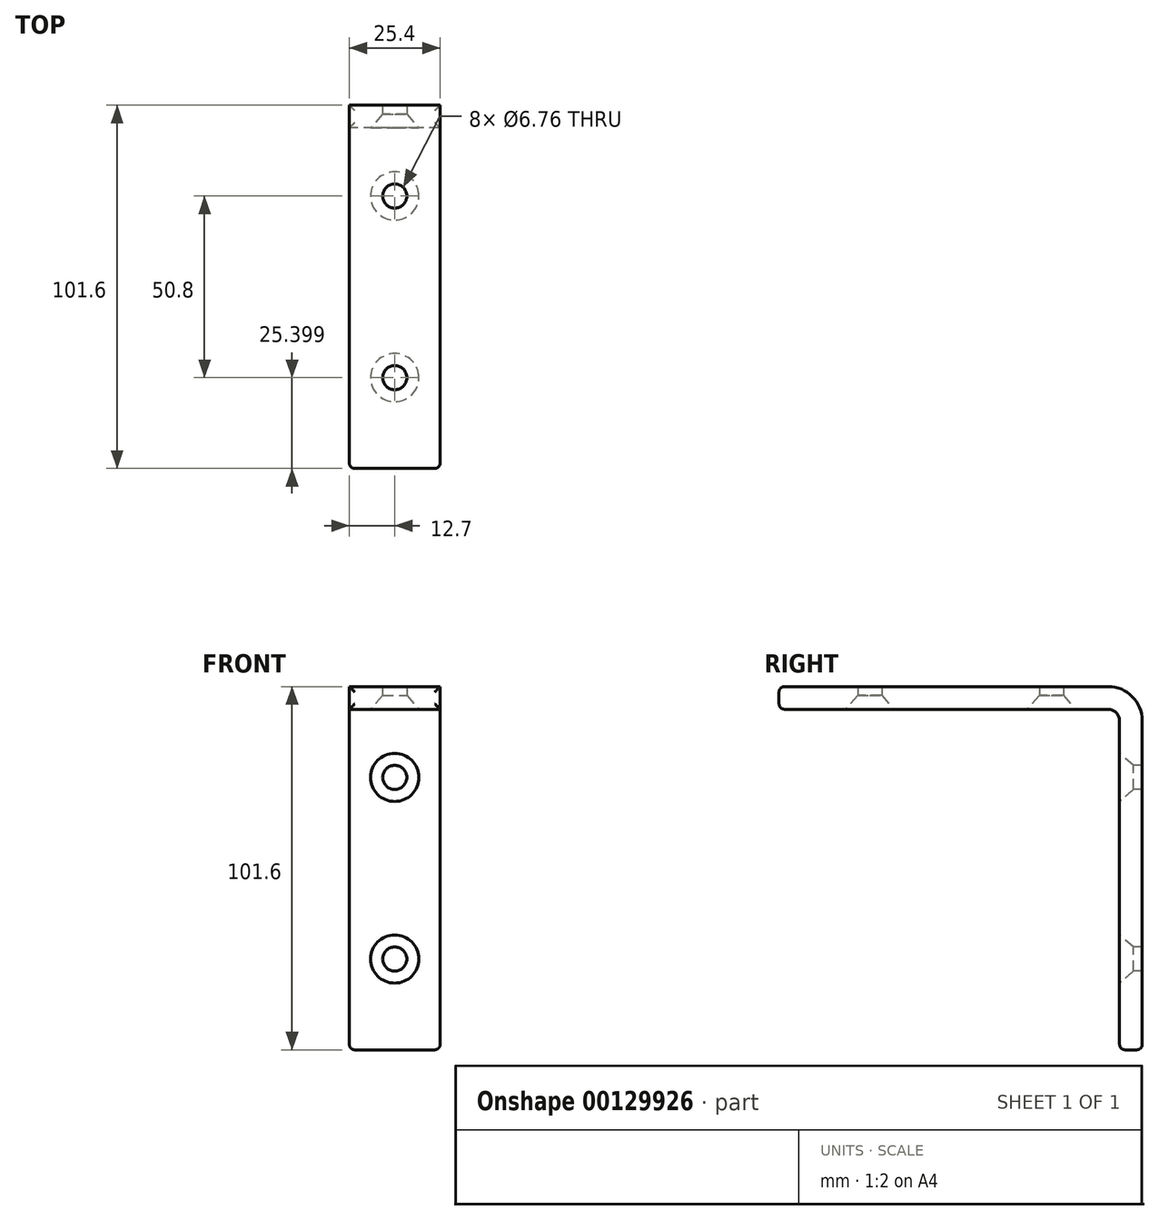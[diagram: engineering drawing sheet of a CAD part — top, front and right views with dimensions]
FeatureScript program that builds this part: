
annotation { "Feature Type Name" : "Feature", "Feature Type Description" : "" }
export const myFeature = defineFeature(function(context is Context, id is Id, definition is map)
    precondition{}
    {
        {
            var Q0;
            Q0=qCreatedBy(makeId("Right.planeOp"),FACE);
            var sketch = newSketch(context, id + "F0", { "sketchPlane" : qUnion([Q0])});
            skLineSegment(sketch, "E0", {"start": v(-36.08, 9.65) * mm, "end": v(59.17, 9.65) * mm});
            skLineSegment(sketch, "E1", {"start": v(59.17, 9.65) * mm, "end": v(59.17, -85.6) * mm});
            skLineSegment(sketch, "E2.0", {"start": v(-36.08, 16) * mm, "end": v(65.52, 16) * mm});
            skLineSegment(sketch, "E3.0", {"start": v(65.52, 16) * mm, "end": v(65.52, -85.6) * mm});
            skLineSegment(sketch, "E4", {"start": v(-36.08, 16) * mm, "end": v(-36.08, 9.65) * mm});
            skLineSegment(sketch, "E5", {"start": v(59.17, -85.6) * mm, "end": v(65.52, -85.6) * mm});
            skSolve(sketch);
        }
        {
            var Q0;
            Q0=makeQuery(id+"F0.imprint","IMPRINT",FACE,{"disambiguationData":[TD([[makeQuery(id+"F0.imprint","IMPRINT",EDGE,{"derivedFrom":sQuery(id+"F0.wireOp",EDGE,"E0")}),1.0]])]});
            extrude(context, id + "F1", {"entities" : qUnion([Q0]), "endBound" : BoundingType.SYMMETRIC, "depth" : 25.4 * mm});
        }
        {
            var Q0;
            Q0=makeQuery(id+"F1.opExtrude","SWEPT_FACE",FACE,{"disambiguationData":[OSD([sQuery(id+"F0.wireOp",EDGE,"E1")])]});
            var sketch = newSketch(context, id + "F2", { "sketchPlane" : qUnion([Q0])});
            skCircle(sketch, "E6", {"center": v(0, -9.4) * mm, "radius": 2.32 * mm});
            skCircle(sketch, "E7", {"center": v(0, -60.2) * mm, "radius": 3.49 * mm});
            skSolve(sketch);
        }
        {
            var Q0;
            Q0=sQuery(id+"F2.wireOp",VERTEX,"E6.center");
            var Q1;
            Q1=sQuery(id+"F2.wireOp",VERTEX,"E7.center");
            var Q2;
            Q2=makeQuery(id+"F1.opExtrude","SWEPT_BODY",BODY,{"disambiguationData":[OSD([sQuery(id+"F0.wireOp",EDGE,"E0"),sQuery(id+"F0.wireOp",EDGE,"E1"),sQuery(id+"F0.wireOp",EDGE,"E2.0"),sQuery(id+"F0.wireOp",EDGE,"E3.0"),sQuery(id+"F0.wireOp",EDGE,"E4"),sQuery(id+"F0.wireOp",EDGE,"E5")])]});
            hole(context, id + "F3", {"style" : HoleStyle.C_SINK, "endStyle" : HoleEndStyle.THROUGH, "standardTappedOrClearance" : lookupTablePath({ "standard" : "ANSI", "fit" : "Normal (ASME)", "size" : "1/4", "type" : "Clearance" }), "standardBlindInLast" : lookupTablePath({ "fit" : "Free", "standard" : "ANSI", "size" : "1/4", "type" : "Clearance" }), "holeDiameter" : 6.76 * mm, "cSinkDiameter" : 13.5 * mm, "cSinkAngle" : 82 * degree, "startFromSketch" : true, "locations" : qUnion([Q0, Q1]), "scope" : qUnion([Q2]), "isTappedThrough" : true});
        }
        {
            var Q0;
            Q0=makeQuery(id+"F1.opExtrude","SWEPT_FACE",FACE,{"disambiguationData":[OSD([sQuery(id+"F0.wireOp",EDGE,"E0")])]});
            var sketch = newSketch(context, id + "F4", { "sketchPlane" : qUnion([Q0])});
            skCircle(sketch, "E8", {"center": v(0, 10.68) * mm, "radius": 4.11 * mm});
            skCircle(sketch, "E9", {"center": v(0, -40.12) * mm, "radius": 3.68 * mm});
            skSolve(sketch);
        }
        {
            var Q0;
            Q0=sQuery(id+"F4.wireOp",VERTEX,"E8.center");
            var Q1;
            Q1=sQuery(id+"F4.wireOp",VERTEX,"E9.center");
            var Q2;
            Q2=makeQuery(id+"F1.opExtrude","SWEPT_BODY",BODY,{"disambiguationData":[OSD([sQuery(id+"F0.wireOp",EDGE,"E0"),sQuery(id+"F0.wireOp",EDGE,"E1"),sQuery(id+"F0.wireOp",EDGE,"E2.0"),sQuery(id+"F0.wireOp",EDGE,"E3.0"),sQuery(id+"F0.wireOp",EDGE,"E4"),sQuery(id+"F0.wireOp",EDGE,"E5")])]});
            hole(context, id + "F5", {"style" : HoleStyle.C_SINK, "endStyle" : HoleEndStyle.THROUGH, "standardTappedOrClearance" : lookupTablePath({ "standard" : "ANSI", "fit" : "Normal (ASME)", "size" : "1/4", "type" : "Clearance" }), "standardBlindInLast" : lookupTablePath({ "fit" : "Free", "standard" : "ANSI", "size" : "1/4", "type" : "Clearance" }), "holeDiameter" : 6.76 * mm, "cSinkDiameter" : 13.5 * mm, "cSinkAngle" : 82 * degree, "startFromSketch" : true, "locations" : qUnion([Q0, Q1]), "scope" : qUnion([Q2]), "isTappedThrough" : true});
        }
        {
            var Q0;
            Q0=makeQuery(id+"F1.opExtrude","SWEPT_EDGE",EDGE,{"disambiguationData":[OSD([sQuery(id+"F0.wireOp",EDGE,"E0"),sQuery(id+"F0.wireOp",EDGE,"E1")])]});
            fillet(context, id + "F6", {"entities" : qUnion([Q0]), "radius" : 3.17 * mm, "tangentPropagation" : true, "allowEdgeOverflow" : false});
        }
        {
            var Q0;
            Q0=makeQuery(id+"F1.opExtrude","SWEPT_EDGE",EDGE,{"disambiguationData":[OSD([sQuery(id+"F0.wireOp",EDGE,"E2.0"),sQuery(id+"F0.wireOp",EDGE,"E3.0")])]});
            fillet(context, id + "F7", {"entities" : qUnion([Q0]), "radius" : 9.52 * mm, "tangentPropagation" : true, "allowEdgeOverflow" : false});
        }
        {
            var Q0;
            Q0=makeQuery(id+"F1.opExtrude","CAP_EDGE",EDGE,{"disambiguationData":[OSD([sQuery(id+"F0.wireOp",EDGE,"E5")])],"isStart":false});
            var Q1;
            Q1=makeQuery(id+"F1.opExtrude","CAP_EDGE",EDGE,{"disambiguationData":[OSD([sQuery(id+"F0.wireOp",EDGE,"E4")])],"isStart":false});
            var Q2;
            Q2=makeQuery(id+"F1.opExtrude","CAP_EDGE",EDGE,{"disambiguationData":[OSD([sQuery(id+"F0.wireOp",EDGE,"E4")])],"isStart":true});
            var Q3;
            Q3=makeQuery(id+"F1.opExtrude","CAP_EDGE",EDGE,{"disambiguationData":[OSD([sQuery(id+"F0.wireOp",EDGE,"E5")])],"isStart":true});
            var Q4;
            Q4=makeQuery(id+"F1.opExtrude","SWEPT_EDGE",EDGE,{"disambiguationData":[OSD([sQuery(id+"F0.wireOp",EDGE,"E3.0"),sQuery(id+"F0.wireOp",EDGE,"E5")])]});
            var Q5;
            Q5=makeQuery(id+"F1.opExtrude","SWEPT_EDGE",EDGE,{"disambiguationData":[OSD([sQuery(id+"F0.wireOp",EDGE,"E2.0"),sQuery(id+"F0.wireOp",EDGE,"E4")])]});
            var Q6;
            Q6=makeQuery(id+"F1.opExtrude","SWEPT_EDGE",EDGE,{"disambiguationData":[OSD([sQuery(id+"F0.wireOp",EDGE,"E0"),sQuery(id+"F0.wireOp",EDGE,"E4")])]});
            var Q7;
            Q7=makeQuery(id+"F1.opExtrude","SWEPT_EDGE",EDGE,{"disambiguationData":[OSD([sQuery(id+"F0.wireOp",EDGE,"E1"),sQuery(id+"F0.wireOp",EDGE,"E5")])]});
            fillet(context, id + "F8", {"entities" : qUnion([Q0, Q1, Q2, Q3, Q4, Q5, Q6, Q7]), "radius" : 1.52 * mm, "tangentPropagation" : true, "allowEdgeOverflow" : false});
        }
    });
